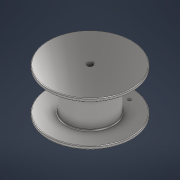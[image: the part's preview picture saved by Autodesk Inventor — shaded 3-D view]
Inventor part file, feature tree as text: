
AUTODESK INVENTOR PART (.ipt)
format: ipt  version: 2021 (Build 250183000, 183)  size: 235,008 bytes
history: native  units: mm
features: sketch x4, fillet x2, extrude x2, revolve x1, hole x1, other x1, chamfer x1
ambient origin geometry x8: Origin, YZ Plane, XZ Plane, XY Plane, X Axis, Y Axis, Z Axis, Center Point
bodies: Solid1 (feature_tree)
feature tree (12):
  revolve  "Revolution1"  [1 undecoded]
  fillet  "Fillet1"  Radius=66.0mm
  fillet  "Fillet2"  Radius=36.0mm
  extrude  "Extrusion1"  TaperAngle=90.0deg  [1 undecoded]
  hole  "Hole1"  [1 undecoded]
  other  "midPlane"
  extrude  "Extrusion2"  Depth=2.0mm
  chamfer  "Chamfer1"  Distance=3.0mm
  sketch  "Sketch1"  dims[d0=5.0mm d1=5.0mm d2=66.0mm d3=36.0mm]
  sketch  "Sketch2"  dims[d4=60.0mm d5=90.0deg]
  sketch  "Sketch3"  dims[d6=2.0mm d7=1.0mm]
  sketch  "Sketch4"  dims[d8=9.0mm d9=5.8mm d10=3.0mm d11=14.0mm d12=0.0mm d13=50.0mm d14=50.0mm d15=50.0mm d16=5.0mm d17=8.0mm d18=3.023mm d19=2.0mm d20=14.3117mm d21=8.0mm d22=0.0mm d23=22.0mm d24=7.5mm d25=0.0mm d26=0.5mm d27=2.0mm d28=45.0deg]
note: 3 required parameter values undecoded (feature->parameter linkage not recoverable at this tier; creation-order binding heuristic only, values carry confidence <= 0.55)